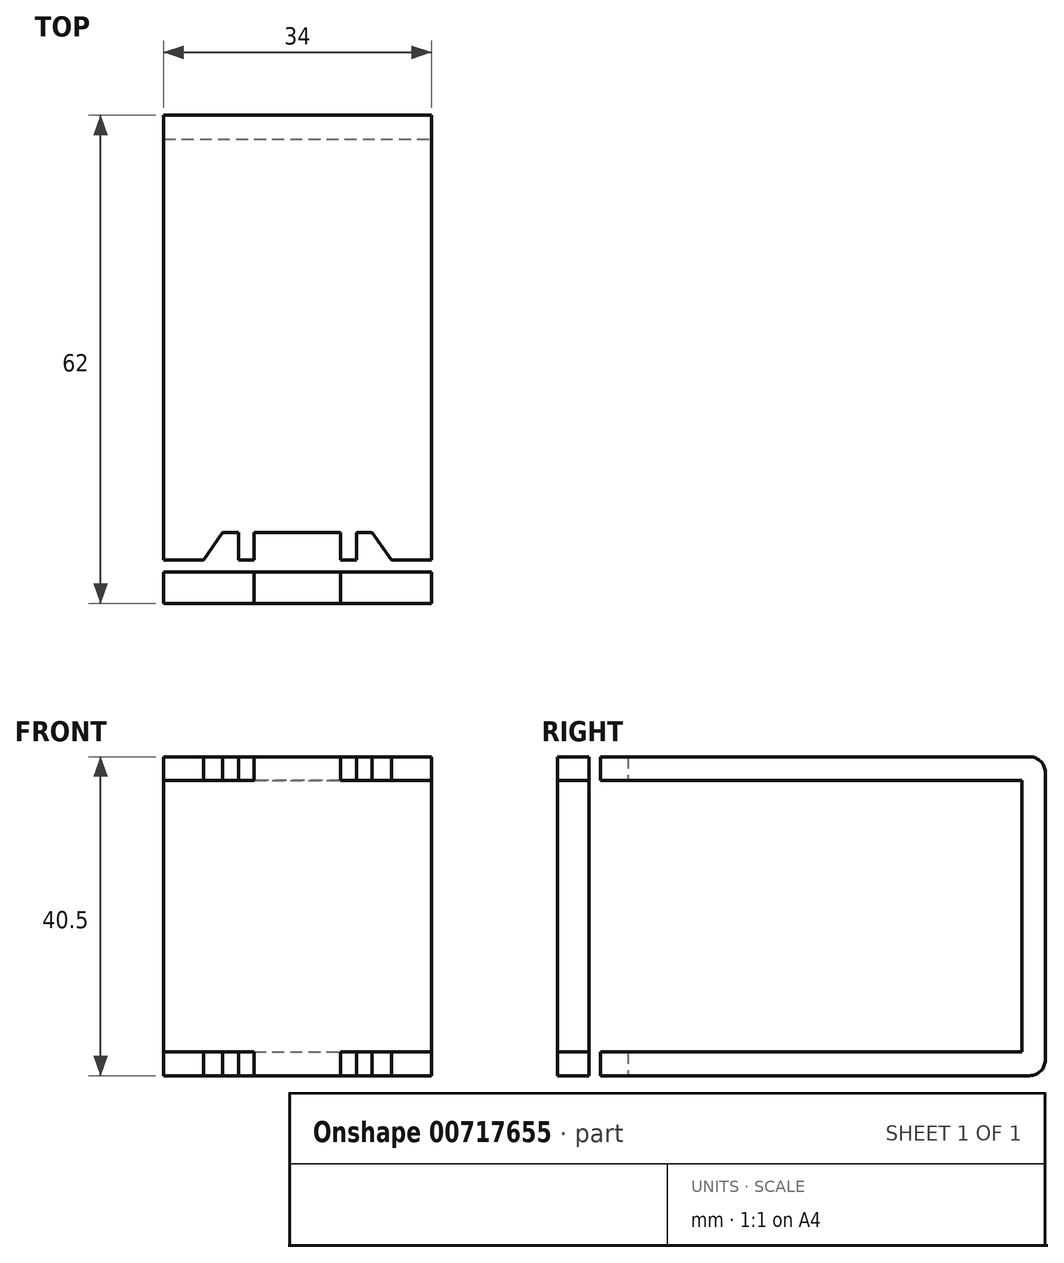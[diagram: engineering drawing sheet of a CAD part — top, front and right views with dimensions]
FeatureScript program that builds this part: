
annotation { "Feature Type Name" : "Feature", "Feature Type Description" : "" }
export const myFeature = defineFeature(function(context is Context, id is Id, definition is map)
    precondition{}
    {
        {
            assignVariable(context, id + "F0", {"name" : "FrameWidth", "anyValue" : 34});
        }
        {
            assignVariable(context, id + "F1", {"name" : "CframeThick", "anyValue" : 3});
        }
        {
            var Q0;
            Q0=qCreatedBy(makeId("Top.planeOp"),FACE);
            var sketch = newSketch(context, id + "F2", { "sketchPlane" : qUnion([Q0])});
            skLineSegment(sketch, "E0.bottom", {"start": v(-17, -26.75) * mm, "end": v(17, -26.75) * mm});
            skLineSegment(sketch, "E0.top", {"start": v(-17, 26.75) * mm, "end": v(17, 26.75) * mm});
            skLineSegment(sketch, "E0.left", {"start": v(-17, -26.75) * mm, "end": v(-17, 26.75) * mm});
            skLineSegment(sketch, "E0.right", {"start": v(17, -26.75) * mm, "end": v(17, 26.75) * mm});
            skPoint(sketch, "E0.middle", {"position": v(0, 0) * mm});
            skLineSegment(sketch, "E1.bottom", {"start": v(-5.5, -30.25) * mm, "end": v(5.5, -30.25) * mm});
            skLineSegment(sketch, "E1.top", {"start": v(-5.5, -23.25) * mm, "end": v(5.5, -23.25) * mm});
            skLineSegment(sketch, "E1.left", {"start": v(-5.5, -30.25) * mm, "end": v(-5.5, -23.25) * mm});
            skLineSegment(sketch, "E1.right", {"start": v(5.5, -30.25) * mm, "end": v(5.5, -23.25) * mm});
            skPoint(sketch, "E1.middle", {"position": v(0, -26.75) * mm});
            skLineSegment(sketch, "E2", {"start": v(-7.5, -23.25) * mm, "end": v(-7.5, -26.75) * mm});
            skLineSegment(sketch, "E3", {"start": v(-7.5, -23.25) * mm, "end": v(-9.5, -23.25) * mm});
            skLineSegment(sketch, "E4", {"start": v(-9.5, -23.25) * mm, "end": v(-11.95, -26.75) * mm});
            skLineSegment(sketch, "E5", {"start": v(0, -26.75) * mm, "end": v(0, 29.13) * mm, "construction": true});
            skLineSegment(sketch, "E6.MirrorCS", {"start": v(9.5, -23.25) * mm, "end": v(11.95, -26.75) * mm});
            skLineSegment(sketch, "E7.MirrorCS", {"start": v(7.5, -23.25) * mm, "end": v(9.5, -23.25) * mm});
            skLineSegment(sketch, "E8.MirrorCS", {"start": v(7.5, -23.25) * mm, "end": v(7.5, -26.75) * mm});
            skSolve(sketch);
        }
        {
            var Q0;
            Q0=qCreatedBy(makeId("Top.planeOp"),FACE);
            cPlane(context, id + "F3", {"entities" : qUnion([Q0]), "cplaneType" : CPlaneType.OFFSET, "offset" : (getVariable(context, 'FrameWidth') + getVariable(context, 'CframeThick') + 0.5) * mm, "width" : 150 * mm, "height" : 150 * mm});
        }
        {
            var Q0;
            Q0=qCreatedBy(id+"F3.planeOp",FACE);
            var sketch = newSketch(context, id + "F4", { "sketchPlane" : qUnion([Q0])});
            skLineSegment(sketch, "E9.0.0", {"start": v(7.5, -26.75) * mm, "end": v(7.5, -23.25) * mm});
            skLineSegment(sketch, "E9.0.1", {"start": v(7.5, -23.25) * mm, "end": v(9.5, -23.25) * mm});
            skLineSegment(sketch, "E9.0.2", {"start": v(9.5, -23.25) * mm, "end": v(11.95, -26.75) * mm});
            skLineSegment(sketch, "E9.0.3", {"start": v(11.95, -26.75) * mm, "end": v(17, -26.75) * mm});
            skLineSegment(sketch, "E9.0.4", {"start": v(17, -26.75) * mm, "end": v(17, 26.75) * mm});
            skLineSegment(sketch, "E9.0.5", {"start": v(17, 26.75) * mm, "end": v(-17, 26.75) * mm});
            skLineSegment(sketch, "E9.0.6", {"start": v(-17, 26.75) * mm, "end": v(-17, -26.75) * mm});
            skLineSegment(sketch, "E9.0.7", {"start": v(-17, -26.75) * mm, "end": v(-11.95, -26.75) * mm});
            skLineSegment(sketch, "E9.0.8", {"start": v(-11.95, -26.75) * mm, "end": v(-9.5, -23.25) * mm});
            skLineSegment(sketch, "E9.0.9", {"start": v(-9.5, -23.25) * mm, "end": v(-7.5, -23.25) * mm});
            skLineSegment(sketch, "E9.0.10", {"start": v(-7.5, -23.25) * mm, "end": v(-7.5, -26.75) * mm});
            skLineSegment(sketch, "E9.0.11", {"start": v(-7.5, -26.75) * mm, "end": v(-5.5, -26.75) * mm});
            skLineSegment(sketch, "E9.0.12", {"start": v(-5.5, -26.75) * mm, "end": v(-5.5, -23.25) * mm});
            skLineSegment(sketch, "E9.0.13", {"start": v(-5.5, -23.25) * mm, "end": v(5.5, -23.25) * mm});
            skLineSegment(sketch, "E9.0.14", {"start": v(5.5, -23.25) * mm, "end": v(5.5, -26.75) * mm});
            skLineSegment(sketch, "E9.0.15", {"start": v(5.5, -26.75) * mm, "end": v(7.5, -26.75) * mm});
            skSolve(sketch);
        }
        {
            var Q0;
            Q0=makeQuery(id+"F2.imprint","IMPRINT",FACE,{"disambiguationData":[TD([[makeQuery(id+"F2.imprint","IMPRINT",EDGE,{"derivedFrom":sQuery(id+"F2.wireOp",EDGE,"E0.top")}),-1.0]])]});
            var Q1;
            Q1=makeQuery(id+"F4.imprint","IMPRINT",FACE,{"disambiguationData":[TD([[makeQuery(id+"F4.imprint","IMPRINT",EDGE,{"derivedFrom":sQuery(id+"F4.wireOp",EDGE,"E9.0.0")}),1.0]])]});
            extrude(context, id + "F5", {"entities" : qUnion([Q0, Q1]), "depth" : (getVariable(context, 'CframeThick')) * mm, "offsetDistance" : 25 * mm});
        }
        {
            var Q0;
            Q0=makeQuery(id+"F5.opExtrude","SWEPT_FACE",FACE,{"disambiguationData":[OSD([sQuery(id+"F2.wireOp",EDGE,"E0.top")])]});
            cPlane(context, id + "F6", {"entities" : qUnion([Q0]), "cplaneType" : CPlaneType.OFFSET, "offset" : 0 * mm, "width" : 150 * mm, "height" : 150 * mm});
        }
        {
            var Q0;
            Q0=qCreatedBy(id+"F6.planeOp",FACE);
            var sketch = newSketch(context, id + "F7", { "sketchPlane" : qUnion([Q0])});
            skLineSegment(sketch, "E10", {"start": v(-17, 0) * mm, "end": v(-17, 40.5) * mm});
            skLineSegment(sketch, "E11", {"start": v(-17, 40.5) * mm, "end": v(17, 40.5) * mm});
            skLineSegment(sketch, "E12", {"start": v(17, 40.5) * mm, "end": v(17, 0) * mm});
            skLineSegment(sketch, "E13", {"start": v(17, 0) * mm, "end": v(-17, 0) * mm});
            skSolve(sketch);
        }
        {
            var Q0;
            Q0=makeQuery(id+"F7.imprint","IMPRINT",FACE,{"disambiguationData":[TD([[makeQuery(id+"F7.imprint","IMPRINT",EDGE,{"derivedFrom":sQuery(id+"F7.wireOp",EDGE,"E10")}),-1.0]])]});
            extrude(context, id + "F8", {"entities" : qUnion([Q0]), "operationType" : NewBodyOperationType.ADD, "depth" : (getVariable(context, 'CframeThick')) * mm, "offsetDistance" : 25 * mm});
        }
        {
            var Q0;
            Q0=makeQuery(id+"F8.opExtrude","CAP_EDGE",EDGE,{"disambiguationData":[OSD([sQuery(id+"F7.wireOp",EDGE,"E11")])],"isStart":false});
            var Q1;
            Q1=makeQuery(id+"F8.opExtrude","CAP_EDGE",EDGE,{"disambiguationData":[OSD([sQuery(id+"F7.wireOp",EDGE,"E13")])],"isStart":false});
            fillet(context, id + "F9", {"entities" : qUnion([Q0, Q1]), "radius" : 2 * mm, "tangentPropagation" : true, "allowEdgeOverflow" : false});
        }
        {
            var Q0;
            Q0=makeQuery(id+"F5.opExtrude","SWEPT_FACE",FACE,{"disambiguationData":[OSD([sQuery(id+"F2.wireOp",EDGE,"E1.top")])]});
            cPlane(context, id + "F10", {"entities" : qUnion([Q0]), "cplaneType" : CPlaneType.OFFSET, "offset" : 5 * mm, "width" : 150 * mm, "height" : 150 * mm});
        }
        {
            var Q0;
            Q0=qCreatedBy(id+"F10.planeOp",FACE);
            var sketch = newSketch(context, id + "F11", { "sketchPlane" : qUnion([Q0])});
            skLineSegment(sketch, "E14.0.0", {"start": v(-5.5, 37.5) * mm, "end": v(5.5, 37.5) * mm});
            skLineSegment(sketch, "E14.0.1", {"start": v(5.5, 37.5) * mm, "end": v(5.5, 40.5) * mm});
            skLineSegment(sketch, "E14.0.2", {"start": v(5.5, 40.5) * mm, "end": v(-5.5, 40.5) * mm});
            skLineSegment(sketch, "E14.0.3", {"start": v(-5.5, 40.5) * mm, "end": v(-5.5, 37.5) * mm});
            skLineSegment(sketch, "E15.0.0", {"start": v(-5.5, 0) * mm, "end": v(5.5, 0) * mm});
            skLineSegment(sketch, "E15.0.1", {"start": v(5.5, 0) * mm, "end": v(5.5, 3) * mm});
            skLineSegment(sketch, "E15.0.2", {"start": v(5.5, 3) * mm, "end": v(-5.5, 3) * mm});
            skLineSegment(sketch, "E15.0.3", {"start": v(-5.5, 3) * mm, "end": v(-5.5, 0) * mm});
            skLineSegment(sketch, "E16.0.0", {"start": v(-17, 37.5) * mm, "end": v(-17, 3) * mm});
            skLineSegment(sketch, "E16.0.1", {"start": v(-17, 3) * mm, "end": v(17, 3) * mm});
            skLineSegment(sketch, "E16.0.2", {"start": v(17, 3) * mm, "end": v(17, 37.5) * mm});
            skLineSegment(sketch, "E16.0.3", {"start": v(17, 37.5) * mm, "end": v(-17, 37.5) * mm});
            skSolve(sketch);
        }
        {
            var Q0;
            {var subQ0=sQuery(id+"F11.wireOp",EDGE,"E14.0.1");Q0=makeQuery(id+"F11.imprint","IMPRINT",FACE,{"disambiguationData":[TD([[makeQuery(id+"F11.imprint","IMPRINT",EDGE,{"derivedFrom":subQ0}),1.0]])]});}
            var Q1;
            {var subQ4=sQuery(id+"F11.wireOp",EDGE,"E16.0.0");Q1=makeQuery(id+"F11.imprint","IMPRINT",FACE,{"disambiguationData":[TD([[makeQuery(id+"F11.imprint","IMPRINT",EDGE,{"derivedFrom":subQ4}),1.0]])]});}
            var Q2;
            Q2=makeQuery(id+"F11.imprint","IMPRINT",FACE,{"disambiguationData":[TD([[makeQuery(id+"F11.imprint","IMPRINT",EDGE,{"derivedFrom":sQuery(id+"F11.wireOp",EDGE,"E15.0.0")}),1.0]])]});
            extrude(context, id + "F12", {"entities" : qUnion([Q0, Q1, Q2]), "operationType" : NewBodyOperationType.ADD, "depth" : (getVariable(context, 'CframeThick') + 1) * mm, "offsetDistance" : 25 * mm});
        }
    });
